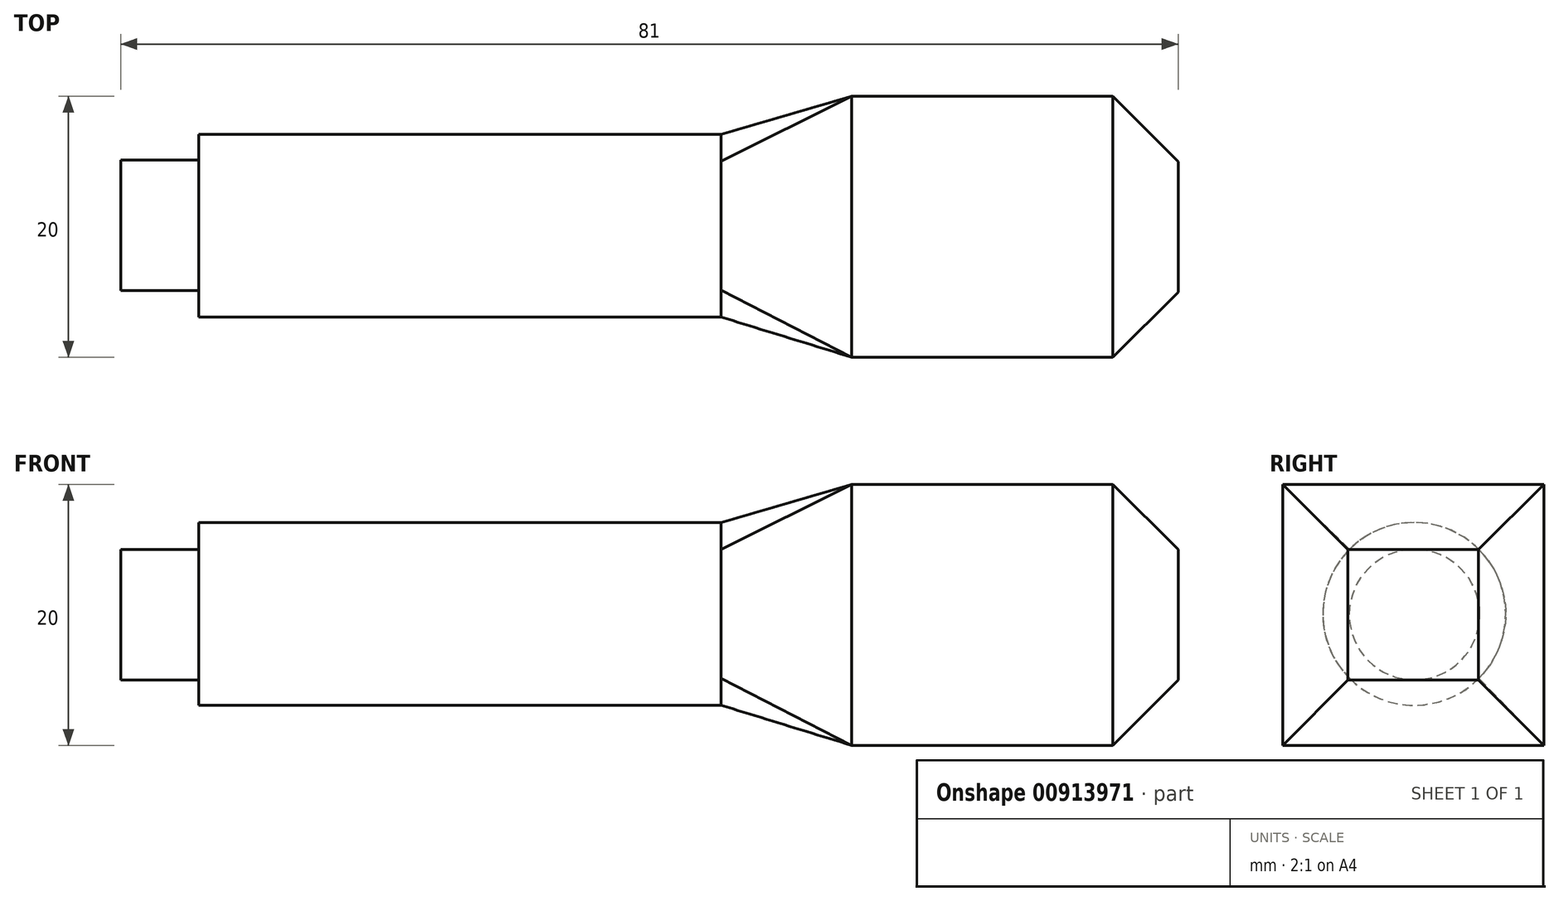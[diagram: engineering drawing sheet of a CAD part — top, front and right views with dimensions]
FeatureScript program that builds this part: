
annotation { "Feature Type Name" : "Feature", "Feature Type Description" : "" }
export const myFeature = defineFeature(function(context is Context, id is Id, definition is map)
    precondition{}
    {
        {
            var Q0;
            Q0=qCreatedBy(makeId("Front.planeOp"),FACE);
            var sketch = newSketch(context, id + "F0", { "sketchPlane" : qUnion([Q0])});
            skLineSegment(sketch, "E0.bottom", {"start": v(-19.73, 17.97) * mm, "end": v(5.27, 17.97) * mm});
            skLineSegment(sketch, "E0.top", {"start": v(-19.73, -2.03) * mm, "end": v(5.27, -2.03) * mm});
            skLineSegment(sketch, "E0.left", {"start": v(-19.73, 17.97) * mm, "end": v(-19.73, -2.03) * mm});
            skLineSegment(sketch, "E0.right", {"start": v(5.27, 17.97) * mm, "end": v(5.27, -2.03) * mm});
            skLineSegment(sketch, "E1", {"start": v(5.27, 7.97) * mm, "end": v(-19.73, 7.97) * mm, "construction": true});
            skLineSegment(sketch, "E2", {"start": v(-19.73, 7.97) * mm, "end": v(-95, 7.97) * mm, "construction": true});
            skSolve(sketch);
        }
        {
            var Q0;
            Q0=makeQuery(id+"F0.imprint","IMPRINT",FACE,{"disambiguationData":[TD([[makeQuery(id+"F0.imprint","IMPRINT",EDGE,{"derivedFrom":sQuery(id+"F0.wireOp",EDGE,"E0.bottom")}),-1.0]])]});
            extrude(context, id + "F1", {"entities" : qUnion([Q0]), "depth" : 20 * mm, "offsetDistance" : 25 * mm});
        }
        {
            var Q0;
            Q0=makeQuery(id+"F1.opExtrude","SWEPT_FACE",FACE,{"disambiguationData":[OSD([sQuery(id+"F0.wireOp",EDGE,"E0.right")])]});
            chamfer(context, id + "F2", {"entities" : qUnion([Q0]), "width" : 5 * mm, "tangentPropagation" : true});
        }
        {
            var Q0;
            Q0=makeQuery(id+"F1.opExtrude","SWEPT_FACE",FACE,{"disambiguationData":[OSD([sQuery(id+"F0.wireOp",EDGE,"E0.left")])]});
            cPlane(context, id + "F3", {"entities" : qUnion([Q0]), "cplaneType" : CPlaneType.OFFSET, "offset" : 10 * mm, "width" : 150 * mm, "height" : 150 * mm});
        }
        {
            var Q0;
            Q0=qCreatedBy(id+"F3.planeOp",FACE);
            var sketch = newSketch(context, id + "F4", { "sketchPlane" : qUnion([Q0])});
            skCircle(sketch, "E3", {"center": v(9.92, 8.05) * mm, "radius": 7 * mm});
            skSolve(sketch);
        }
        {
            var Q0;
            Q0=makeQuery(id+"F4.imprint","IMPRINT",FACE,{"disambiguationData":[TD([[makeQuery(id+"F4.imprint","IMPRINT",EDGE,{"derivedFrom":sQuery(id+"F4.wireOp",EDGE,"E3")}),1.0]])]});
            extrude(context, id + "F5", {"entities" : qUnion([Q0]), "depth" : 40 * mm, "offsetDistance" : 25 * mm});
        }
        {
            var Q1;
            Q1=makeQuery(id+"F5.opExtrude","CAP_FACE",FACE,{"disambiguationData":[OSD([sQuery(id+"F4.wireOp",EDGE,"E3")])],"isStart":true});
            var Q2;
            Q2=makeQuery(id+"F1.opExtrude","SWEPT_FACE",FACE,{"disambiguationData":[OSD([sQuery(id+"F0.wireOp",EDGE,"E0.left")])]});
            loft(context, id + "F6", {"operationType" : NewBodyOperationType.ADD, "sheetProfilesArray" : [{ "sheetProfileEntities" : qUnion([Q1]) }, { "sheetProfileEntities" : qUnion([Q2]) }]});
        }
        {
            var Q0;
            Q0=makeQuery(id+"F5.opExtrude","CAP_FACE",FACE,{"disambiguationData":[OSD([sQuery(id+"F4.wireOp",EDGE,"E3")])],"isStart":false});
            var sketch = newSketch(context, id + "F7", { "sketchPlane" : qUnion([Q0])});
            skCircle(sketch, "E4", {"center": v(9.9, 8) * mm, "radius": 5 * mm});
            skSolve(sketch);
        }
        {
            var Q0;
            Q0=makeQuery(id+"F7.imprint","IMPRINT",FACE,{"disambiguationData":[TD([[makeQuery(id+"F7.imprint","IMPRINT",EDGE,{"derivedFrom":sQuery(id+"F7.wireOp",EDGE,"E4")}),1.0]])]});
            extrude(context, id + "F8", {"entities" : qUnion([Q0]), "operationType" : NewBodyOperationType.ADD, "depth" : 6 * mm, "offsetDistance" : 25 * mm});
        }
    });
